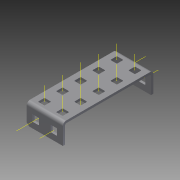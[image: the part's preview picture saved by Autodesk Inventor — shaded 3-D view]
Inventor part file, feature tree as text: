
AUTODESK INVENTOR PART (.ipt)
format: ipt  version: 2015 (Build 190159000, 159)  size: 2,385,920 bytes
history: native  units: in
note: dims shown in document units (in); Inventor stores cm internally (conversion verified against a paired STEP export)
features: other x20, pattern_linear x2, sheet_metal_op x1, extrude x1, imported_body x1, sketch x1
ambient origin geometry x8: Origin, YZ Plane, XZ Plane, XY Plane, X Axis, Y Axis, Z Axis, Center Point
bodies: Body1 (feature_tree)
feature tree (26):
  sheet_metal_op  "Fold1"
  other  "C-Channel"
  extrude  "length cut"  Depth=0.5in
  other  "top axis"
  other  "front axis"
  other  "back axis"
  pattern_linear  "top axes"  Spacing1=0.5in  [1 undecoded]
  pattern_linear  "horiz axes"  Spacing1=0.0in  [1 undecoded]
  other  "right plane"
  imported_body  "Base1"
  sketch  "Sketch1"  dims[d1=0.0in d4=0.5in d5=1.9685in d7=0.5in d10=0.5in d11=0.0in d12=0.0in d13=0.0in d14=-1.0in d15=0.0in d16=0.0in]
  other  "Work Point1"
  other  "Work Axis6"
  other  "Work Axis11"
  other  "Work Axis16"
  other  "Work Axis21"
  other  "Work Point2"
  other  "Work Point3"
  other  "Work Axis36"
  other  "Work Axis60"
  other  "Work Axis84"
  other  "Work Axis108"
  other  "Work Axis132"
  other  "Work Axis156"
  other  "Work Axis180"
  other  "left plane"
note: 2 required parameter values undecoded (feature->parameter linkage not recoverable at this tier; creation-order binding heuristic only, values carry confidence <= 0.55)
